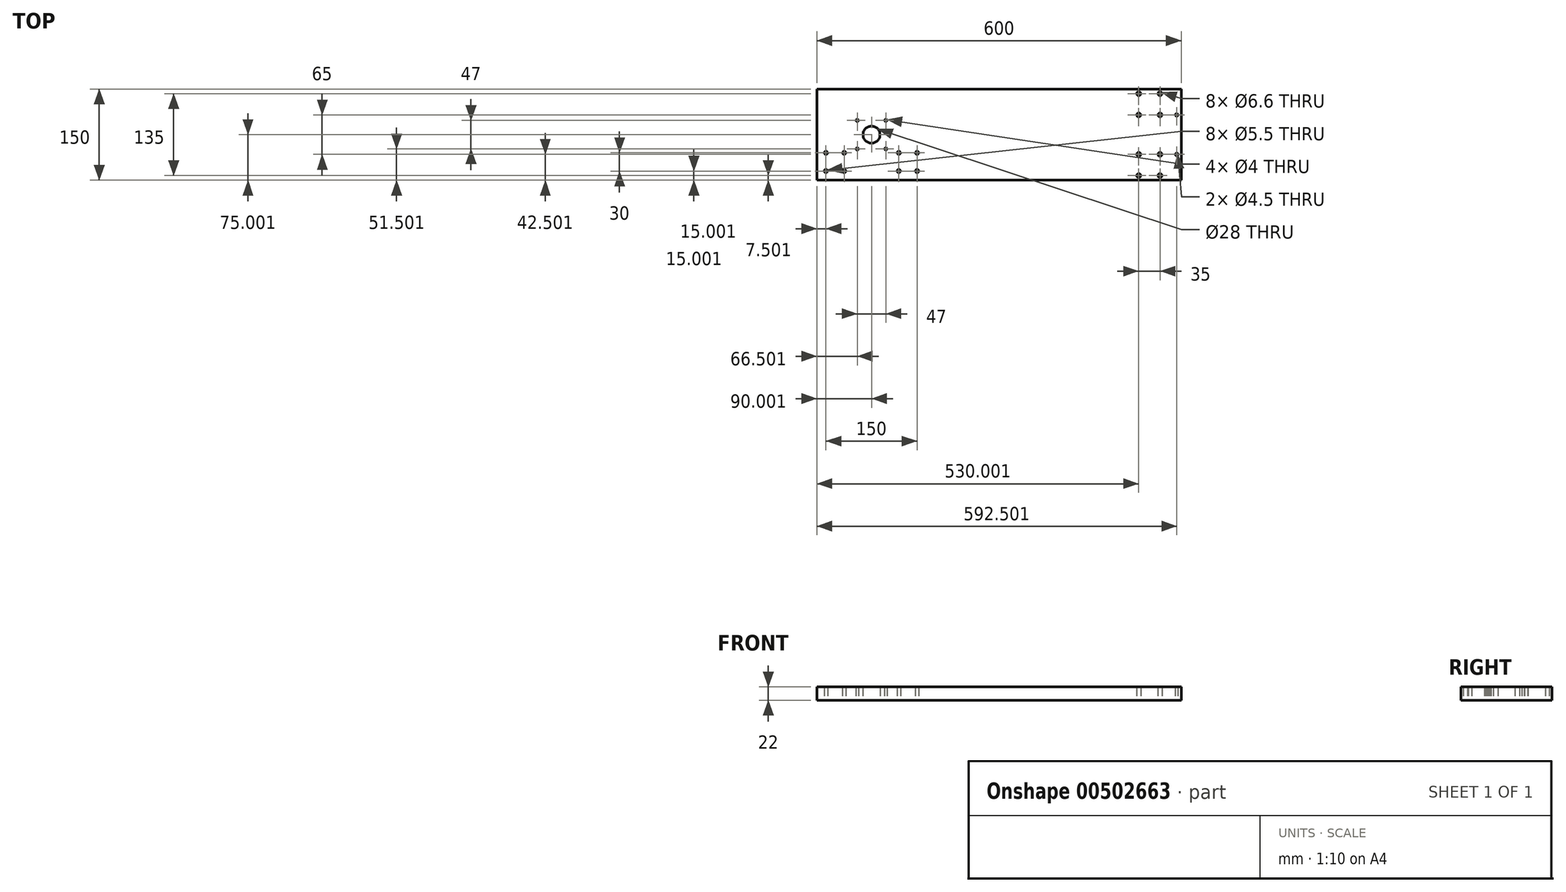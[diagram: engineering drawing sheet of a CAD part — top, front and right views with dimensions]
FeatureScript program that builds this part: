
annotation { "Feature Type Name" : "Feature", "Feature Type Description" : "" }
export const myFeature = defineFeature(function(context is Context, id is Id, definition is map)
    precondition{}
    {
        {
            var Q0;
            Q0=qCreatedBy(makeId("Top.planeOp"),FACE);
            var sketch = newSketch(context, id + "F0", { "sketchPlane" : qUnion([Q0])});
            skLineSegment(sketch, "E0", {"start": v(-30.95, 156.47) * mm, "end": v(569.05, 156.47) * mm});
            skLineSegment(sketch, "E1", {"start": v(569.05, 156.47) * mm, "end": v(569.05, 6.47) * mm});
            skLineSegment(sketch, "E2", {"start": v(569.05, 6.47) * mm, "end": v(-30.95, 6.47) * mm});
            skLineSegment(sketch, "E3", {"start": v(-30.95, 6.47) * mm, "end": v(-30.95, 156.47) * mm});
            skPoint(sketch, "E4", {"position": v(534.05, 13.97) * mm});
            skPoint(sketch, "E5", {"position": v(499.05, 13.97) * mm});
            skPoint(sketch, "E6", {"position": v(499.05, 48.97) * mm});
            skPoint(sketch, "E7", {"position": v(534.05, 48.97) * mm});
            skPoint(sketch, "E8", {"position": v(534.05, 113.97) * mm});
            skPoint(sketch, "E9", {"position": v(499.05, 113.97) * mm});
            skPoint(sketch, "E10", {"position": v(499.05, 148.97) * mm});
            skPoint(sketch, "E11", {"position": v(534.05, 148.97) * mm});
            skPoint(sketch, "E12", {"position": v(561.55, 113.97) * mm});
            skPoint(sketch, "E13", {"position": v(561.55, 48.97) * mm});
            skPoint(sketch, "E14", {"position": v(-15.95, 21.47) * mm});
            skPoint(sketch, "E15", {"position": v(14.05, 21.47) * mm});
            skPoint(sketch, "E16", {"position": v(14.05, 51.47) * mm});
            skPoint(sketch, "E17", {"position": v(-15.95, 51.47) * mm});
            skPoint(sketch, "E18", {"position": v(104.05, 21.47) * mm});
            skPoint(sketch, "E19", {"position": v(134.05, 21.47) * mm});
            skPoint(sketch, "E20", {"position": v(134.05, 51.47) * mm});
            skPoint(sketch, "E21", {"position": v(104.05, 51.47) * mm});
            skPoint(sketch, "E22", {"position": v(59.05, 81.47) * mm});
            skPoint(sketch, "E23", {"position": v(82.55, 104.97) * mm});
            skPoint(sketch, "E24", {"position": v(35.55, 104.97) * mm});
            skPoint(sketch, "E25", {"position": v(35.55, 57.97) * mm});
            skPoint(sketch, "E26", {"position": v(82.55, 57.97) * mm});
            skSolve(sketch);
        }
        {
            var Q0;
            Q0=makeQuery(id+"F0.imprint","IMPRINT",FACE,{"disambiguationData":[TD([[makeQuery(id+"F0.imprint","IMPRINT",EDGE,{"derivedFrom":sQuery(id+"F0.wireOp",EDGE,"E0")}),-1.0]])]});
            extrude(context, id + "F1", {"entities" : qUnion([Q0]), "depth" : 22 * mm, "offsetDistance" : 25 * mm});
        }
        {
            var Q0;
            Q0=sQuery(id+"F0.wireOp",VERTEX,"E9");
            var Q1;
            Q1=sQuery(id+"F0.wireOp",VERTEX,"E8");
            var Q2;
            Q2=sQuery(id+"F0.wireOp",VERTEX,"E10");
            var Q3;
            Q3=sQuery(id+"F0.wireOp",VERTEX,"E11");
            var Q4;
            Q4=sQuery(id+"F0.wireOp",VERTEX,"E4");
            var Q5;
            Q5=sQuery(id+"F0.wireOp",VERTEX,"E6");
            var Q6;
            Q6=sQuery(id+"F0.wireOp",VERTEX,"E5");
            var Q7;
            Q7=sQuery(id+"F0.wireOp",VERTEX,"E7");
            var Q8;
            Q8=makeQuery(id+"F1.opExtrude","SWEPT_BODY",BODY,{"disambiguationData":[OSD([sQuery(id+"F0.wireOp",EDGE,"E0"),sQuery(id+"F0.wireOp",EDGE,"E1"),sQuery(id+"F0.wireOp",EDGE,"E2"),sQuery(id+"F0.wireOp",EDGE,"E3")])]});
            hole(context, id + "F2", {"style" : HoleStyle.SIMPLE, "endStyle" : HoleEndStyle.THROUGH, "oppositeDirection" : true, "holeDiameter" : 6.6 * mm, "isTappedThrough" : true, "tappedDepth" : 12 * mm, "tapClearance" : 3, "locations" : qUnion([Q0, Q1, Q2, Q3, Q4, Q5, Q6, Q7]), "scope" : qUnion([Q8])});
        }
        {
            var Q0;
            Q0=sQuery(id+"F0.wireOp",VERTEX,"E14");
            var Q1;
            Q1=sQuery(id+"F0.wireOp",VERTEX,"E15");
            var Q2;
            Q2=sQuery(id+"F0.wireOp",VERTEX,"E21");
            var Q3;
            Q3=sQuery(id+"F0.wireOp",VERTEX,"E18");
            var Q4;
            Q4=sQuery(id+"F0.wireOp",VERTEX,"E16");
            var Q5;
            Q5=sQuery(id+"F0.wireOp",VERTEX,"E20");
            var Q6;
            Q6=sQuery(id+"F0.wireOp",VERTEX,"E19");
            var Q7;
            Q7=sQuery(id+"F0.wireOp",VERTEX,"E17");
            var Q8;
            Q8=makeQuery(id+"F1.opExtrude","SWEPT_BODY",BODY,{"disambiguationData":[OSD([sQuery(id+"F0.wireOp",EDGE,"E0"),sQuery(id+"F0.wireOp",EDGE,"E1"),sQuery(id+"F0.wireOp",EDGE,"E2"),sQuery(id+"F0.wireOp",EDGE,"E3")])]});
            hole(context, id + "F3", {"style" : HoleStyle.SIMPLE, "endStyle" : HoleEndStyle.THROUGH, "oppositeDirection" : true, "holeDiameter" : 5.5 * mm, "isTappedThrough" : true, "tappedDepth" : 12 * mm, "tapClearance" : 3, "locations" : qUnion([Q0, Q1, Q2, Q3, Q4, Q5, Q6, Q7]), "scope" : qUnion([Q8])});
        }
        {
            var Q0;
            Q0=sQuery(id+"F0.wireOp",VERTEX,"E22");
            var Q1;
            Q1=makeQuery(id+"F1.opExtrude","SWEPT_BODY",BODY,{"disambiguationData":[OSD([sQuery(id+"F0.wireOp",EDGE,"E0"),sQuery(id+"F0.wireOp",EDGE,"E1"),sQuery(id+"F0.wireOp",EDGE,"E2"),sQuery(id+"F0.wireOp",EDGE,"E3")])]});
            hole(context, id + "F4", {"style" : HoleStyle.SIMPLE, "endStyle" : HoleEndStyle.THROUGH, "oppositeDirection" : true, "holeDiameter" : 28 * mm, "isTappedThrough" : true, "tappedDepth" : 12 * mm, "tapClearance" : 3, "locations" : qUnion([Q0]), "scope" : qUnion([Q1])});
        }
        {
            var Q0;
            Q0=sQuery(id+"F0.wireOp",VERTEX,"E12");
            var Q1;
            Q1=sQuery(id+"F0.wireOp",VERTEX,"E13");
            var Q2;
            Q2=makeQuery(id+"F1.opExtrude","SWEPT_BODY",BODY,{"disambiguationData":[OSD([sQuery(id+"F0.wireOp",EDGE,"E0"),sQuery(id+"F0.wireOp",EDGE,"E1"),sQuery(id+"F0.wireOp",EDGE,"E2"),sQuery(id+"F0.wireOp",EDGE,"E3")])]});
            hole(context, id + "F5", {"style" : HoleStyle.SIMPLE, "endStyle" : HoleEndStyle.THROUGH, "oppositeDirection" : true, "holeDiameter" : 4.5 * mm, "isTappedThrough" : true, "tappedDepth" : 12 * mm, "tapClearance" : 3, "locations" : qUnion([Q0, Q1]), "scope" : qUnion([Q2])});
        }
        {
            var Q0;
            Q0=sQuery(id+"F0.wireOp",VERTEX,"E23");
            var Q1;
            Q1=sQuery(id+"F0.wireOp",VERTEX,"E24");
            var Q2;
            Q2=sQuery(id+"F0.wireOp",VERTEX,"E25");
            var Q3;
            Q3=sQuery(id+"F0.wireOp",VERTEX,"E26");
            var Q4;
            Q4=makeQuery(id+"F1.opExtrude","SWEPT_BODY",BODY,{"disambiguationData":[OSD([sQuery(id+"F0.wireOp",EDGE,"E0"),sQuery(id+"F0.wireOp",EDGE,"E1"),sQuery(id+"F0.wireOp",EDGE,"E2"),sQuery(id+"F0.wireOp",EDGE,"E3")])]});
            hole(context, id + "F6", {"style" : HoleStyle.SIMPLE, "endStyle" : HoleEndStyle.THROUGH, "oppositeDirection" : true, "holeDiameter" : 4 * mm, "isTappedThrough" : true, "tappedDepth" : 12 * mm, "tapClearance" : 3, "locations" : qUnion([Q0, Q1, Q2, Q3]), "scope" : qUnion([Q4])});
        }
    });
